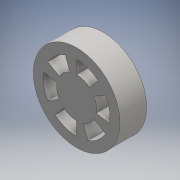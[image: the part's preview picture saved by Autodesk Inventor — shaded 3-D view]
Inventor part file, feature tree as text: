
AUTODESK INVENTOR PART (.ipt)
format: ipt  version: 2016 (Build 200138000, 138)  size: 135,168 bytes
history: native  units: mm
features: extrude x2, sketch x2, pattern_circular x1
ambient origin geometry x8: Origin, YZ Plane, XZ Plane, XY Plane, X Axis, Y Axis, Z Axis, Center Point
bodies: Solid1 (feature_tree)
feature tree (5):
  extrude  "Extrusion1"  Depth=40.0mm TaperAngle=0.0deg
  extrude  "Extrusion2"  Depth=30.0mm
  pattern_circular  "Circular Pattern1"  Count=5  [1 undecoded]
  sketch  "Sketch1"  dims[d0=130.0mm d1=40.0mm d2=0.0mm]
  sketch  "Sketch2"  dims[d4=6.981317mm d5=30.0mm d6=50.0mm d7=10.0mm d8=0.0mm d9=60.0mm d10=360.0deg]
note: 1 required parameter value undecoded (feature->parameter linkage not recoverable at this tier; creation-order binding heuristic only, values carry confidence <= 0.55)
